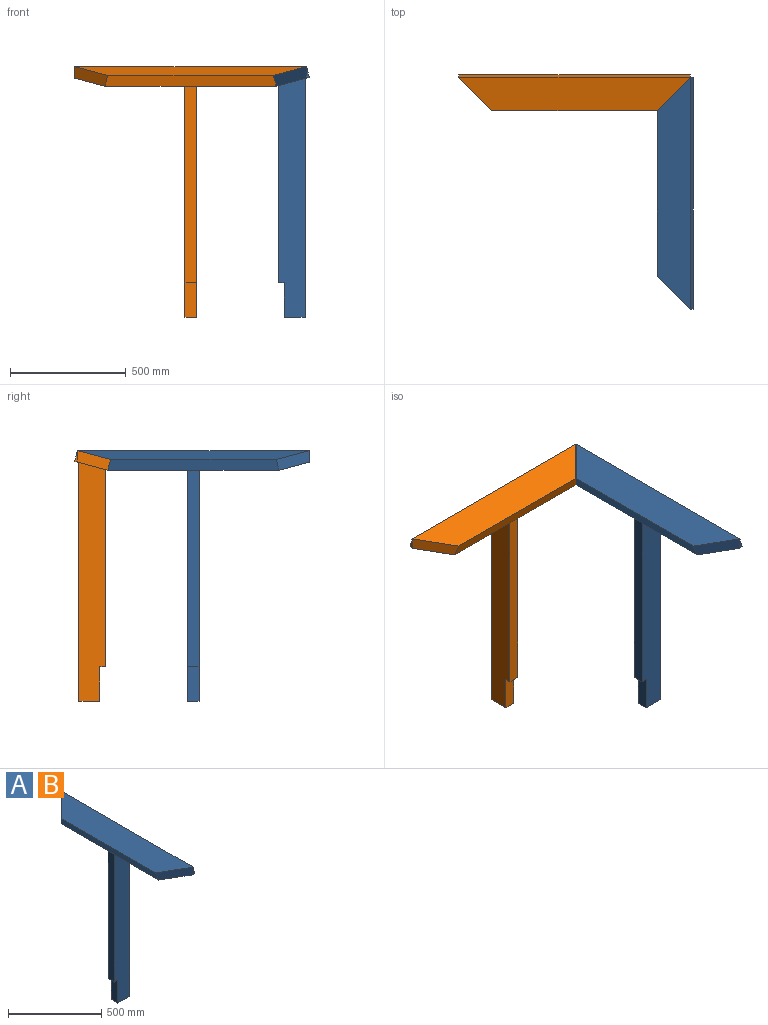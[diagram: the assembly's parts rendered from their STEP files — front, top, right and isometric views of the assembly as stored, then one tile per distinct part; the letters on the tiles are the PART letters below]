
ASSEMBLY  parts=2 mates=1
PART A: 15 faces, bbox 155.4x1000x1082.1 mm
  f0: plane 1000x142.96mm, normal (0.26,0,-0.97), area 124645.2mm2, adj f2,f3,f7,f8,f9,f10,f11,f12
  f1: plane 1000x142.96mm, normal (-0.26,0,0.97), area 126842.4mm2, adj f2,f10,f13,f14
  f2: plane 738.93x46.36mm, normal (-0.97,0,-0.26), area 34872.4mm2, adj f0,f1,f13,f14
  f3: plane 850x48mm, normal (-1,0,0), area 40800mm2, adj f0,f4,f8,f9
  f4: plane 48x25mm, normal (0,0,-1), area 1200mm2, adj f3,f5,f8,f9
  f5: plane 150x48mm, normal (-1,0,0), area 7200mm2, adj f4,f6,f8,f9
  f6: plane 90x48mm, normal (0,0,-1), area 4320mm2, adj f5,f7,f8,f9
  f7: plane 1030.81x48mm, normal (1,0,0), area 49479.1mm2, adj f0,f6,f8,f9
  f8: plane 1030.81x115mm, normal (0,-1,0), area 113021.8mm2, adj f0,f3,f4,f5,f6,f7
  f9: plane 1030.81x115mm, normal (0,1,0), area 113021.8mm2, adj f0,f3,f4,f5,f6,f7
  f10: plane 1000x46.36mm, normal (0.97,0,0.26), area 48000mm2, adj f0,f1,f11,f12
  f11: plane 49.69x12.42mm, normal (0,-1,0), area 308.7mm2, adj f0,f10,f14
  f12: plane 49.69x12.42mm, normal (0,1,0), area 308.7mm2, adj f0,f10,f13
  f13: plane 142.96x142.96mm, normal (-0.71,0.71,0), area 9610mm2, adj f0,f1,f2,f12
  f14: plane 142.96x142.96mm, normal (-0.71,-0.71,0), area 9610mm2, adj f0,f1,f2,f11
PART B: same geometry as A
PLACE A t=(-418.9,-113.88,-247.23)mm
PLACE B rot(axis=(0,0,1),90deg) t=(-798.03,265.25,-247.23)mm
MATE fastened B.f14 <-> A.f13  axis (0.71,-0.71,0) through (-366.45,317.7,642.04)mm
